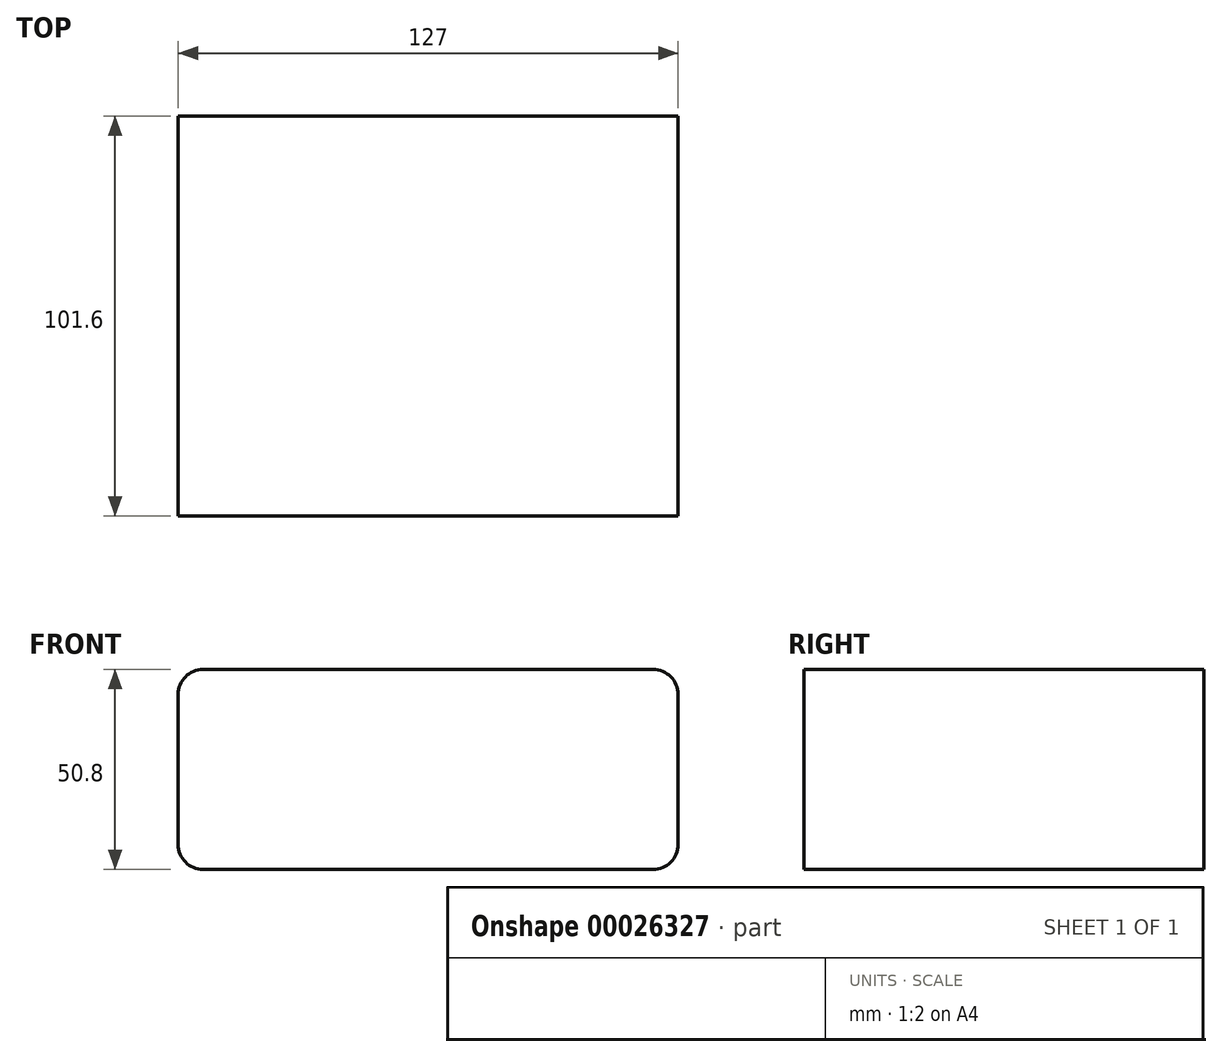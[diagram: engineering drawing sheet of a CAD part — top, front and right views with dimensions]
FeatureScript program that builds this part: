
annotation { "Feature Type Name" : "Feature", "Feature Type Description" : "" }
export const myFeature = defineFeature(function(context is Context, id is Id, definition is map)
    precondition{}
    {
        {
            var Q0;
            Q0=qCreatedBy(makeId("Front.planeOp"),FACE);
            var sketch = newSketch(context, id + "F0", { "sketchPlane" : qUnion([Q0])});
            skLineSegment(sketch, "E0.bottom", {"start": v(-54.82, 56.57) * mm, "end": v(59.48, 56.57) * mm});
            skLineSegment(sketch, "E0.top", {"start": v(-54.82, 5.77) * mm, "end": v(59.48, 5.77) * mm});
            skLineSegment(sketch, "E0.left", {"start": v(-61.17, 50.22) * mm, "end": v(-61.17, 12.12) * mm});
            skLineSegment(sketch, "E0.right", {"start": v(65.83, 50.22) * mm, "end": v(65.83, 12.12) * mm});
            skPoint(sketch, "E1.visualSharp", {"position": v(-61.17, 56.57) * mm});
            skArc(sketch, "E1.filletArc", {"start": v(-54.82, 56.57) * mm, "mid": v(-59.31, 54.71) * mm, "end": v(-61.17, 50.22) * mm});
            skPoint(sketch, "E2.visualSharp", {"position": v(-61.17, 5.77) * mm});
            skArc(sketch, "E2.filletArc", {"start": v(-61.17, 12.12) * mm, "mid": v(-59.31, 7.63) * mm, "end": v(-54.82, 5.77) * mm});
            skPoint(sketch, "E3.visualSharp", {"position": v(65.83, 5.77) * mm});
            skArc(sketch, "E3.filletArc", {"start": v(59.48, 5.77) * mm, "mid": v(63.97, 7.63) * mm, "end": v(65.83, 12.12) * mm});
            skPoint(sketch, "E4.visualSharp", {"position": v(65.83, 56.57) * mm});
            skArc(sketch, "E4.filletArc", {"start": v(65.83, 50.22) * mm, "mid": v(63.97, 54.71) * mm, "end": v(59.48, 56.57) * mm});
            skSolve(sketch);
        }
        {
            var Q0;
            Q0=makeQuery(id+"F0.imprint","IMPRINT",FACE,{"disambiguationData":[TD([[makeQuery(id+"F0.imprint","IMPRINT",EDGE,{"derivedFrom":sQuery(id+"F0.wireOp",EDGE,"E0.bottom")}),-1.0]])]});
            var Q1;
            Q1 = qSketchRegion(id + "F0", true);
            extrude(context, id + "F1", {"entities" : qUnion([Q0, Q1]), "depth" : 101.6 * mm});
        }
    });
